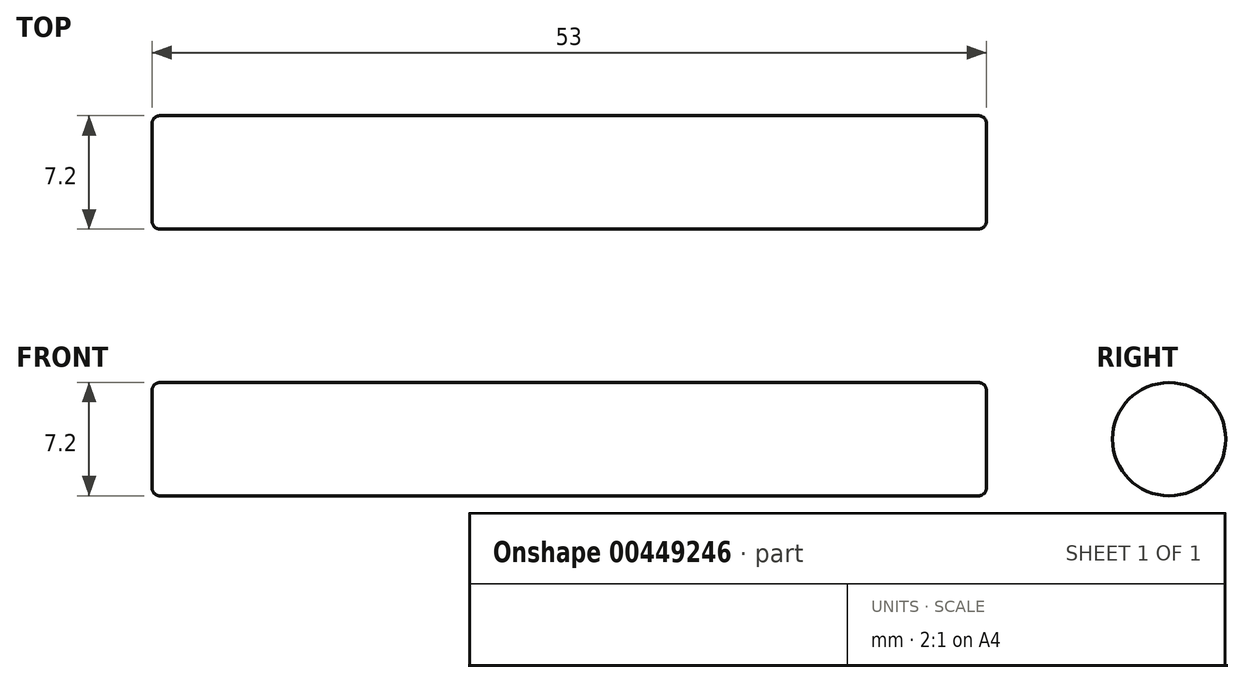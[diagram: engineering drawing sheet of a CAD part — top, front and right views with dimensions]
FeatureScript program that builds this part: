
annotation { "Feature Type Name" : "Feature", "Feature Type Description" : "" }
export const myFeature = defineFeature(function(context is Context, id is Id, definition is map)
    precondition{}
    {
        {
            var Q0;
            Q0=qCreatedBy(makeId("Right.planeOp"),FACE);
            var sketch = newSketch(context, id + "F0", { "sketchPlane" : qUnion([Q0])});
            skCircle(sketch, "E0", {"center": v(0, 0) * mm, "radius": 3.6 * mm});
            skSolve(sketch);
        }
        {
            var Q0;
            Q0 = qSketchRegion(id + "F0", true);
            extrude(context, id + "F1", {"entities" : qUnion([Q0]), "depth" : (23 + 30) * mm});
        }
        {
            var Q0;
            Q0=makeQuery(id+"F1.opExtrude","CAP_FACE",FACE,{"disambiguationData":[OSD([sQuery(id+"F0.wireOp",EDGE,"E0")])],"isStart":false});
            var Q1;
            Q1=makeQuery(id+"F1.opExtrude","CAP_FACE",FACE,{"disambiguationData":[OSD([sQuery(id+"F0.wireOp",EDGE,"E0")])],"isStart":true});
            fillet(context, id + "F2", {"entities" : qUnion([Q0, Q1]), "radius" : .5 * mm, "tangentPropagation" : true, "allowEdgeOverflow" : false});
        }
    });
